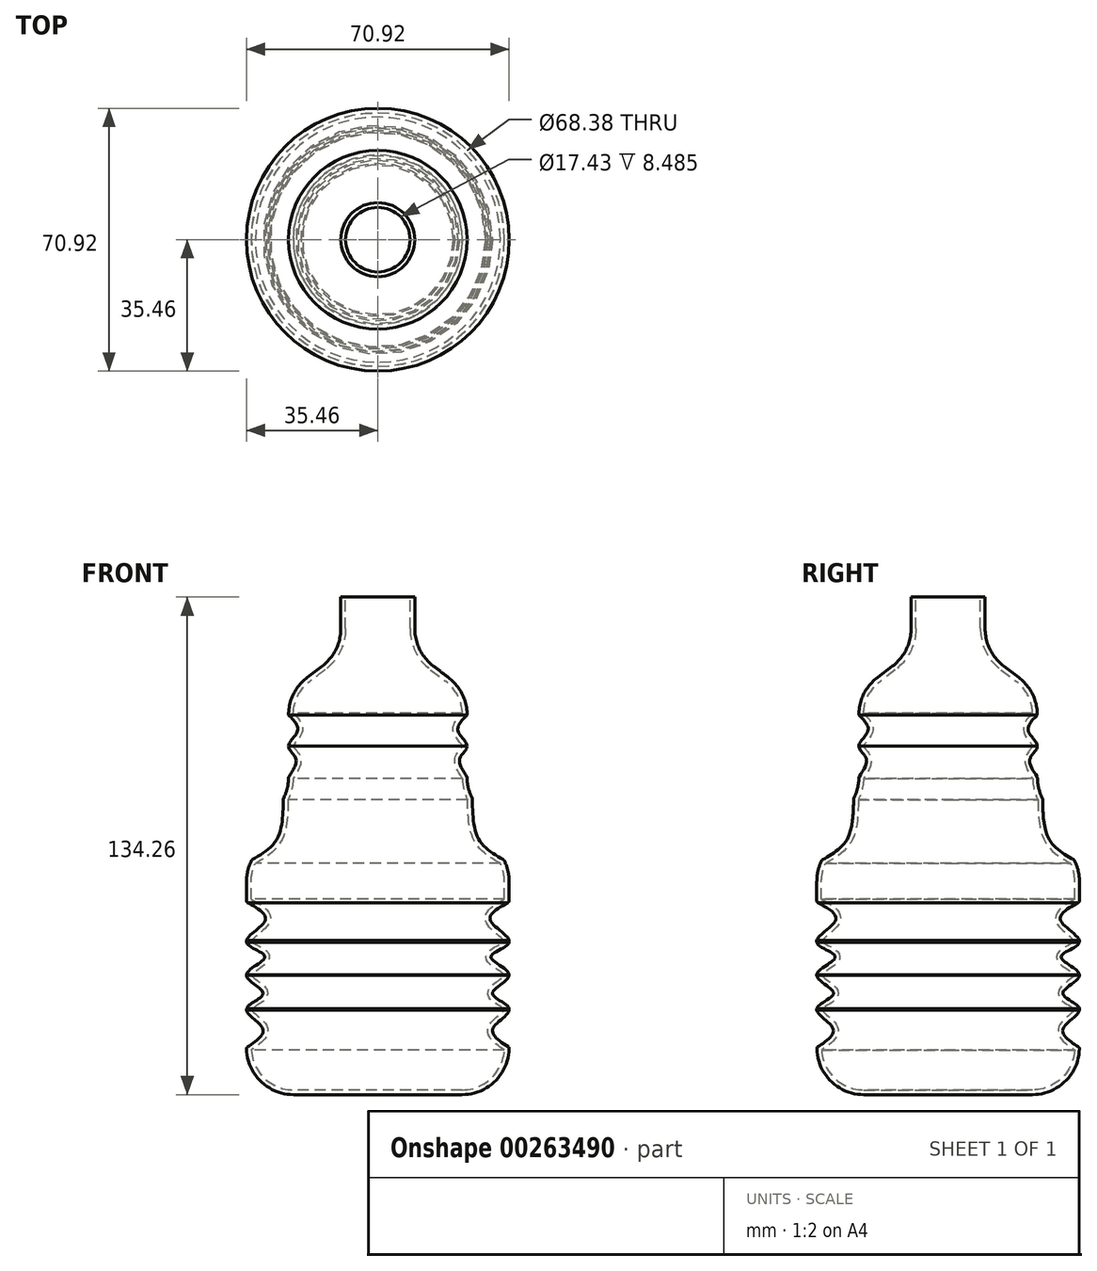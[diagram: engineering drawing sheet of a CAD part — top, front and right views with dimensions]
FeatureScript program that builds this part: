
annotation { "Feature Type Name" : "Feature", "Feature Type Description" : "" }
export const myFeature = defineFeature(function(context is Context, id is Id, definition is map)
    precondition{}
    {
        {
            var Q0;
            Q0=qCreatedBy(makeId("Front.planeOp"),FACE);
            var sketch = newSketch(context, id + "F0", { "sketchPlane" : qUnion([Q0])});
            skLineSegment(sketch, "E0", {"start": v(0, -76.08) * mm, "end": v(-22.76, -76.08) * mm});
            skLineSegment(sketch, "E1", {"start": v(-35.46, -53.3) * mm, "end": v(-35.46, -52.92) * mm});
            skLineSegment(sketch, "E2", {"start": v(-24.1, 17.93) * mm, "end": v(-24.1, 18) * mm});
            skLineSegment(sketch, "E3", {"start": v(-19.06, 36.52) * mm, "end": v(-15.02, 39.57) * mm});
            skLineSegment(sketch, "E4", {"start": v(-9.98, 49.7) * mm, "end": v(-9.98, 58.18) * mm});
            skLineSegment(sketch, "E5", {"start": v(-9.98, 58.18) * mm, "end": v(0, 58.18) * mm});
            skLineSegment(sketch, "E6", {"start": v(0, 58.18) * mm, "end": v(0, -76.08) * mm});
            skPoint(sketch, "E7.visualSharp", {"position": v(-35.46, -76.08) * mm});
            skArc(sketch, "E7.filletArc", {"start": v(-35.46, -63.67) * mm, "mid": v(-31.64, -72.46) * mm, "end": v(-22.76, -76.08) * mm});
            skPoint(sketch, "E8.visualSharp", {"position": v(-35.46, -15.5) * mm});
            skArc(sketch, "E8.filletArc", {"start": v(-34.13, -12.91) * mm, "mid": v(-35.12, -15.66) * mm, "end": v(-35.46, -18.57) * mm});
            skPoint(sketch, "E9.visualSharp", {"position": v(-24.1, 6.54) * mm});
            skArc(sketch, "E9.filletArc", {"start": v(-25.45, 3.92) * mm, "mid": v(-24.46, 6.6) * mm, "end": v(-24.1, 9.45) * mm});
            skPoint(sketch, "E10.visualSharp", {"position": v(-24.1, 32.7) * mm});
            skArc(sketch, "E10.filletArc", {"start": v(-19.06, 36.52) * mm, "mid": v(-22.77, 32.04) * mm, "end": v(-24.1, 26.39) * mm});
            skPoint(sketch, "E11.visualSharp", {"position": v(-9.98, 43.38) * mm});
            skArc(sketch, "E11.filletArc", {"start": v(-15.02, 39.57) * mm, "mid": v(-11.31, 44.04) * mm, "end": v(-9.98, 49.7) * mm});
            skFitSpline(sketch, "E12", {"points": [v(-35.46, -63.38) * mm, v(-31.07, -58.22) * mm, v(-35.46, -52.92) * mm, v(-30.97, -48.73) * mm, v(-35.46, -43.78) * mm, v(-30.52, -38.91) * mm, v(-35.46, -34.97) * mm, v(-30.4, -29.08) * mm, v(-35.46, -24.11) * mm], "startDerivative": vector(61.28, 40.63) * mm, "endDerivative": vector(-68, 36.65) * mm});
            skLineSegment(sketch, "E13.trimOffspring", {"start": v(-35.46, -23.77) * mm, "end": v(-35.46, -18.57) * mm});
            skLineSegment(sketch, "E14.trimOffspring", {"start": v(-35.46, -34.97) * mm, "end": v(-35.46, -34.53) * mm});
            skLineSegment(sketch, "E15.trimOffspring", {"start": v(-35.46, -43.87) * mm, "end": v(-35.46, -43.78) * mm});
            skArc(sketch, "E16.filletArc", {"start": v(-35.46, -23.77) * mm, "mid": v(-35.38, -24.06) * mm, "end": v(-35.16, -24.27) * mm});
            skArc(sketch, "E17.filletArc", {"start": v(-35.23, -63.23) * mm, "mid": v(-35.4, -63.42) * mm, "end": v(-35.46, -63.67) * mm});
            skFitSpline(sketch, "E18", {"points": [v(-24.1, 9.62) * mm, v(-22.14, 14.67) * mm, v(-24.1, 18) * mm, v(-21.64, 22.1) * mm, v(-24.1, 26.39) * mm], "startDerivative": vector(13.65, 20.15) * mm, "endDerivative": vector(-16.55, 16.75) * mm});
            skFitSpline(sketch, "E19", {"points": [v(-34.05, -12.75) * mm, v(-27.28, -7.21) * mm, v(-25.51, 3.8) * mm], "startDerivative": vector(17, 9.7) * mm, "endDerivative": vector(0.4, 23.14) * mm});
            skArc(sketch, "E20.filletArc", {"start": v(-25.45, 3.92) * mm, "mid": v(-25.5, 3.8) * mm, "end": v(-25.51, 3.67) * mm});
            skArc(sketch, "E21.filletArc", {"start": v(-24, 9.77) * mm, "mid": v(-24.07, 9.62) * mm, "end": v(-24.1, 9.45) * mm});
            skArc(sketch, "E22.filletArc", {"start": v(-33.9, -12.67) * mm, "mid": v(-34.03, -12.77) * mm, "end": v(-34.13, -12.91) * mm});
            skSolve(sketch);
        }
        {
            var Q0;
            Q0=makeQuery(id+"F0.imprint","IMPRINT",FACE,{"disambiguationData":[TD([[makeQuery(id+"F0.imprint","IMPRINT",EDGE,{"derivedFrom":sQuery(id+"F0.wireOp",EDGE,"E0")}),-1.0]])]});
            var Q1;
            Q1=sQuery(id+"F0.wireOp",EDGE,"E6");
            revolve(context, id + "F1", {"entities" : qUnion([Q0]), "axis" : qUnion([Q1]), "revolveType" : RevolveType.FULL});
        }
        {
            var Q0;
            Q0=makeQuery(id+"F1.opRevolve","SWEPT_FACE",FACE,{"disambiguationData":[OSD([sQuery(id+"F0.wireOp",EDGE,"E5")])]});
            shell(context, id + "F2", {"entities" : qUnion([Q0]), "thickness" : 1.27 * mm});
        }
    });
